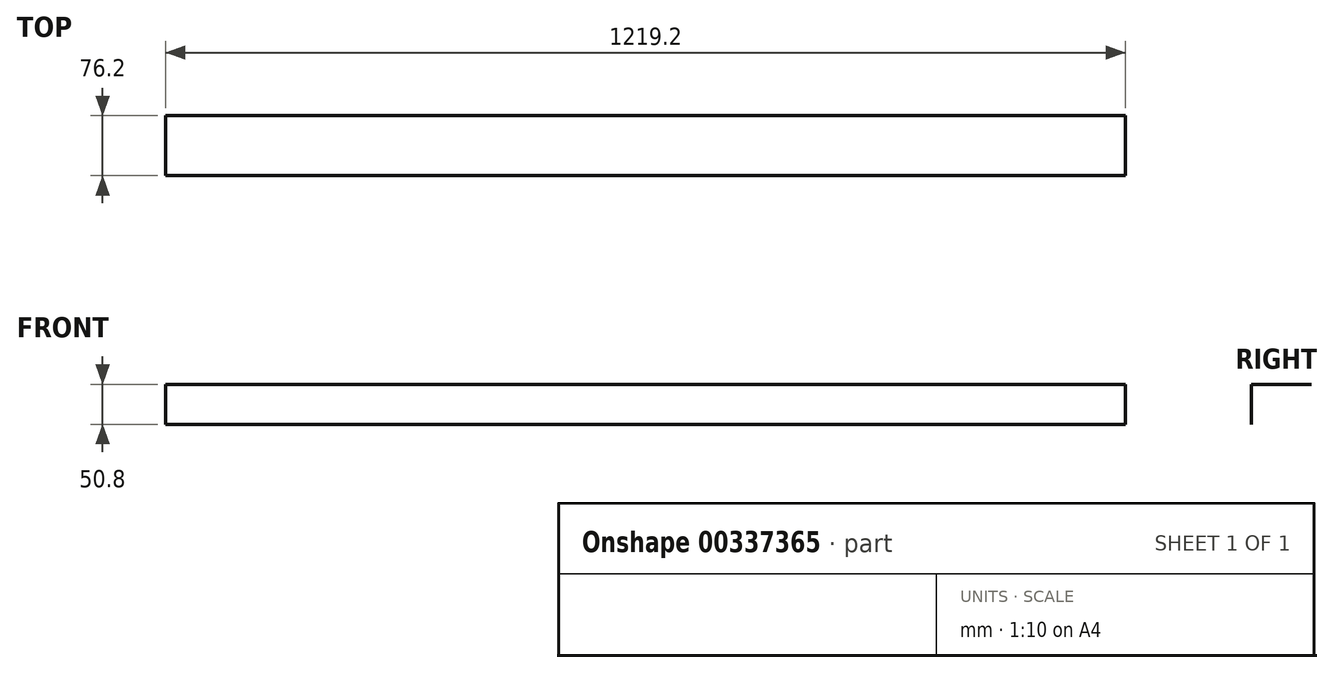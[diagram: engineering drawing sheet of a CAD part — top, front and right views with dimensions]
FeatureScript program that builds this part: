
annotation { "Feature Type Name" : "Feature", "Feature Type Description" : "" }
export const myFeature = defineFeature(function(context is Context, id is Id, definition is map)
    precondition{}
    {
        {
            var Q0;
            Q0=qCreatedBy(makeId("Right.planeOp"),FACE);
            var sketch = newSketch(context, id + "F0", { "sketchPlane" : qUnion([Q0])});
            skLineSegment(sketch, "E0", {"start": v(29.65, -39.09) * mm, "end": v(29.65, 11.71) * mm});
            skLineSegment(sketch, "E1", {"start": v(29.65, 11.71) * mm, "end": v(105.85, 11.71) * mm});
            skSolve(sketch);
        }
        {
            var Q0;
            Q0 = qSketchRegion(id + "F0", true);
            var Q1;
            Q1=sQuery(id+"F0.wireOp",EDGE,"E1");
            var Q2;
            Q2=sQuery(id+"F0.wireOp",EDGE,"E0");
            extrude(context, id + "F1", {"entities" : qUnion([Q0]), "bodyType" : ToolBodyType.SURFACE, "surfaceEntities" : qUnion([Q1, Q2]), "depth" : 1219.2 * mm});
        }
    });
